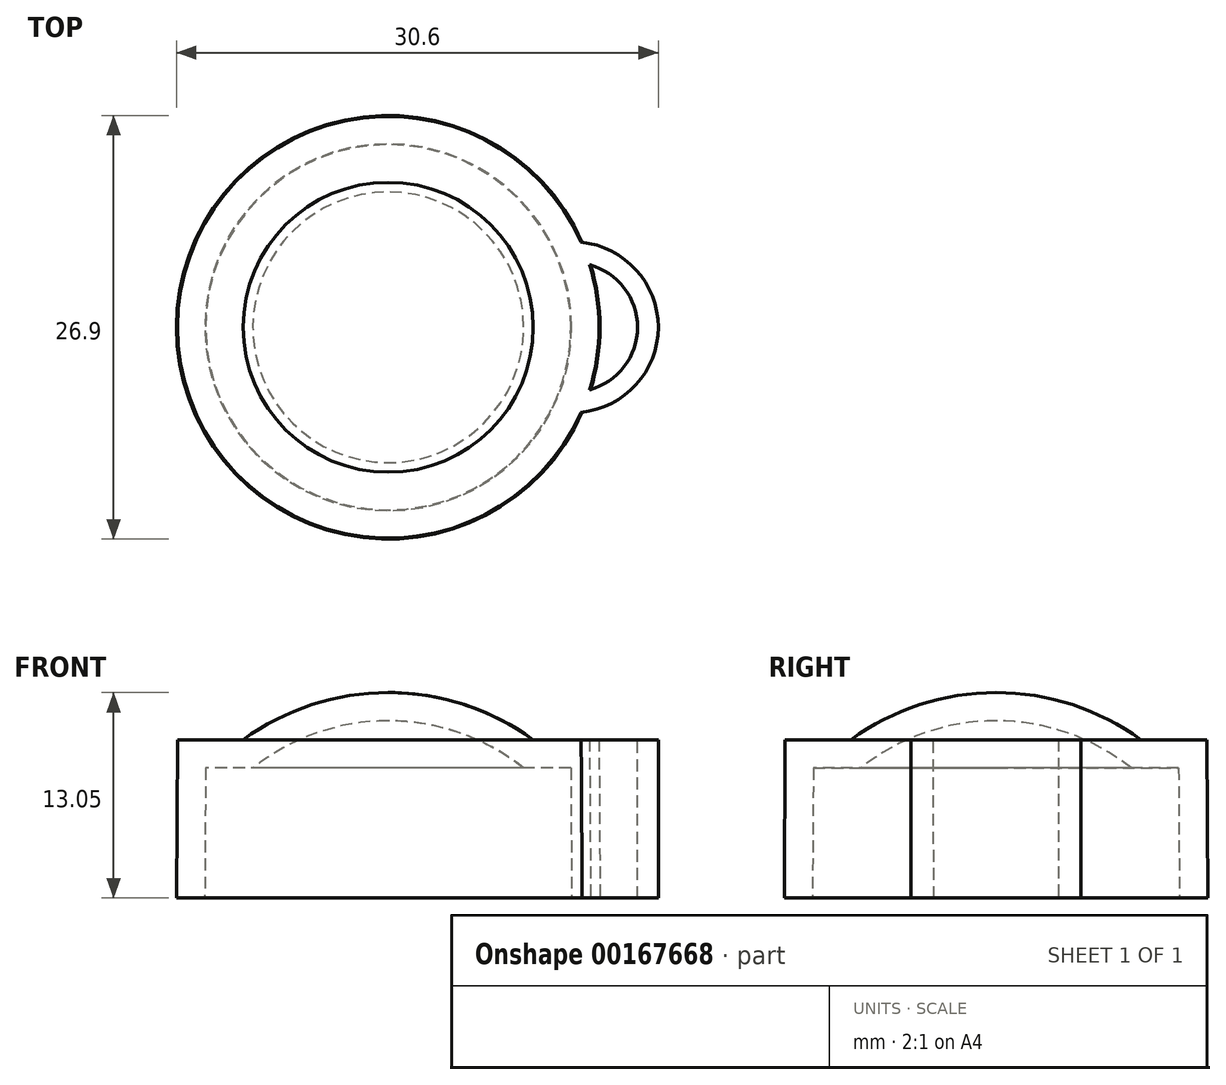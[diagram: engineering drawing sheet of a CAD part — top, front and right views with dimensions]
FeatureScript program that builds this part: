
annotation { "Feature Type Name" : "Feature", "Feature Type Description" : "" }
export const myFeature = defineFeature(function(context is Context, id is Id, definition is map)
    precondition{}
    {
        {
            var Q0;
            Q0=qCreatedBy(makeId("Front.planeOp"),FACE);
            var sketch = newSketch(context, id + "F0", { "sketchPlane" : qUnion([Q0])});
            skLineSegment(sketch, "E0", {"start": v(0, 0) * mm, "end": v(11.65, 0) * mm});
            skLineSegment(sketch, "E1", {"start": v(11.65, 0) * mm, "end": v(11.6, 8.25) * mm});
            skLineSegment(sketch, "E2", {"start": v(11.6, 8.25) * mm, "end": v(0, 8.25) * mm});
            skLineSegment(sketch, "E3", {"start": v(0, 8.25) * mm, "end": v(0, 0) * mm});
            skCircle(sketch, "E4", {"center": v(0, -2.58) * mm, "radius": 13.83 * mm});
            skLineSegment(sketch, "E5", {"start": v(0, 8.25) * mm, "end": v(0, 11.25) * mm});
            skPoint(sketch, "E6", {"position": v(8.6, 8.25) * mm});
            skSolve(sketch);
        }
        {
            var Q0;
            {var subQ0=sQuery(id+"F0.wireOp",EDGE,"E5");Q0=makeQuery(id+"F0.imprint","IMPRINT",FACE,{"disambiguationData":[TD([[makeQuery(id+"F0.imprint","IMPRINT",EDGE,{"derivedFrom":subQ0}),-1.0]])]});}
            var Q1;
            {var subQ5=sQuery(id+"F0.wireOp",EDGE,"E0");Q1=makeQuery(id+"F0.imprint","IMPRINT",FACE,{"disambiguationData":[TD([[makeQuery(id+"F0.imprint","IMPRINT",EDGE,{"derivedFrom":subQ5}),1.0]])]});}
            var Q2;
            {var subQ0=sQuery(id+"F0.wireOp",EDGE,"E2");var subQ1=sQuery(id+"F0.wireOp",EDGE,"E1");var subQ2=makeQuery(id+"F0.imprint","INTERSECT",VERTEX,{"derivedFrom":[subQ1,subQ0]});Q2=makeQuery(id+"F0.imprint","IMPRINT",FACE,{"disambiguationData":[TD([[makeQuery(id+"F0.imprint","IMPRINT",EDGE,{"disambiguationData":[TD([[subQ2,1.0]])],"derivedFrom":subQ1}),1.0]])]});}
            var Q3;
            Q3=sQuery(id+"F0.wireOp",EDGE,"E3");
            revolve(context, id + "F1", {"entities" : qUnion([Q0, Q1, Q2]), "axis" : qUnion([Q3]), "revolveType" : RevolveType.FULL});
        }
        {
            var Q0;
            Q0=makeQuery(id+"F1.opRevolve","SWEPT_FACE",FACE,{"disambiguationData":[OSD([sQuery(id+"F0.wireOp",EDGE,"E0")])]});
            shell(context, id + "F2", {"entities" : qUnion([Q0]), "thickness" : 1.8 * mm, "oppositeDirection" : true});
        }
        {
            var Q0;
            Q0=makeQuery(id+"F1.opRevolve","SWEPT_FACE",FACE,{"disambiguationData":[OSD([sQuery(id+"F0.wireOp",EDGE,"E2")])]});
            var sketch = newSketch(context, id + "F3", { "sketchPlane" : qUnion([Q0])});
            skCircle(sketch, "E7", {"center": v(11.72, 0) * mm, "radius": 4.11 * mm});
            skCircle(sketch, "E8", {"center": v(11.72, 0) * mm, "radius": 5.43 * mm});
            skCircle(sketch, "E9.0", {"center": v(0, 0) * mm, "radius": 13.39 * mm});
            skSolve(sketch);
        }
        {
            var Q0;
            {var subQ0=sQuery(id+"F3.wireOp",EDGE,"E9.0");var subQ1=sQuery(id+"F3.wireOp",EDGE,"E7");var subQ2=makeQuery(id+"F3.imprint","INTERSECT",VERTEX,{"disambiguationData":[OD(0.0)],"derivedFrom":[subQ1,subQ0]});Q0=makeQuery(id+"F3.imprint","IMPRINT",FACE,{"disambiguationData":[TD([[makeQuery(id+"F3.imprint","IMPRINT",EDGE,{"disambiguationData":[TD([[subQ2,1.0]])],"derivedFrom":subQ1}),-1.0]])]});}
            var Q1;
            Q1=makeQuery(id+"F1.opRevolve","SWEPT_FACE",FACE,{"disambiguationData":[OSD([sQuery(id+"F0.wireOp",EDGE,"E0")])]});
            extrude(context, id + "F4", {"entities" : qUnion([Q0]), "operationType" : NewBodyOperationType.ADD, "endBound" : BoundingType.UP_TO_SURFACE, "oppositeDirection" : true, "endBoundEntityFace" : qUnion([Q1]), "depth" : 25 * mm});
        }
    });
